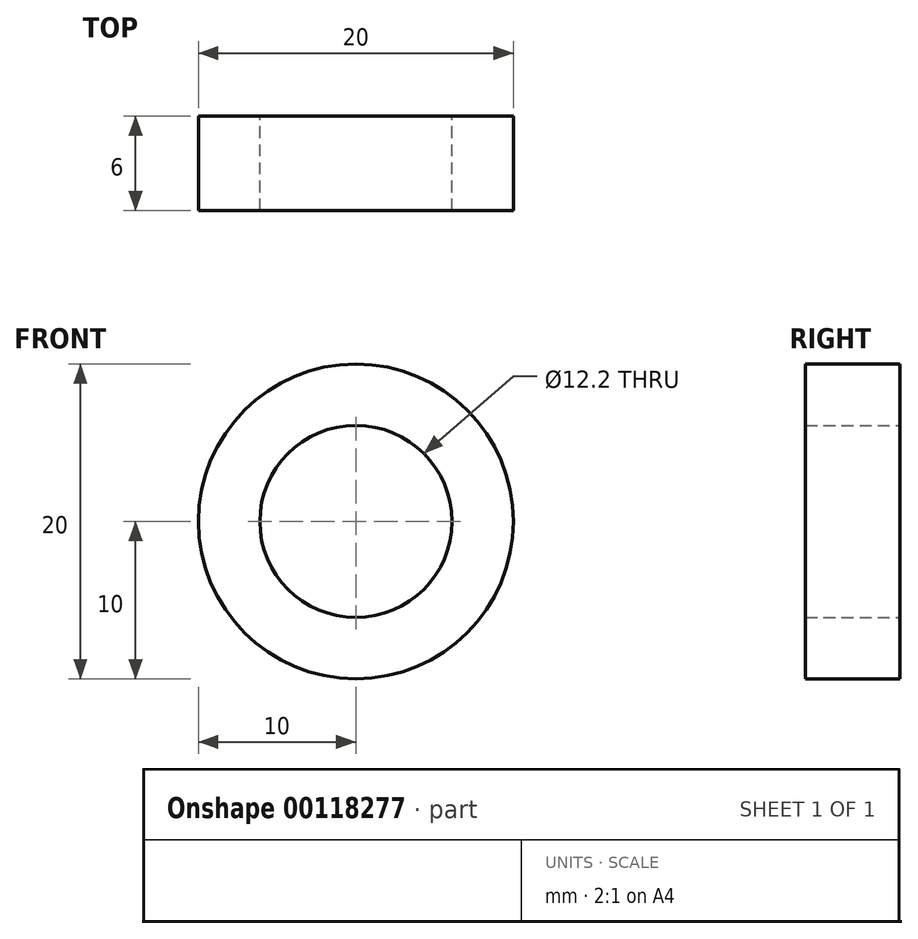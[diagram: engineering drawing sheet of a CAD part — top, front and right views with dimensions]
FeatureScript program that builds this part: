
annotation { "Feature Type Name" : "Feature", "Feature Type Description" : "" }
export const myFeature = defineFeature(function(context is Context, id is Id, definition is map)
    precondition{}
    {
        {
            var Q0;
            Q0=qCreatedBy(makeId("Front.planeOp"),FACE);
            var sketch = newSketch(context, id + "F0", { "sketchPlane" : qUnion([Q0])});
            skCircle(sketch, "E0", {"center": v(0, 0) * mm, "radius": 6.1 * mm});
            skCircle(sketch, "E1", {"center": v(0, 0) * mm, "radius": 10 * mm});
            skSolve(sketch);
        }
        {
            var Q0;
            Q0=makeQuery(id+"F0.imprint","IMPRINT",FACE,{"disambiguationData":[TD([[makeQuery(id+"F0.imprint","IMPRINT",EDGE,{"derivedFrom":sQuery(id+"F0.wireOp",EDGE,"E0")}),-1.0]])]});
            extrude(context, id + "F1", {"entities" : qUnion([Q0]), "endBound" : BoundingType.SYMMETRIC, "depth" : 6 * mm});
        }
    });
